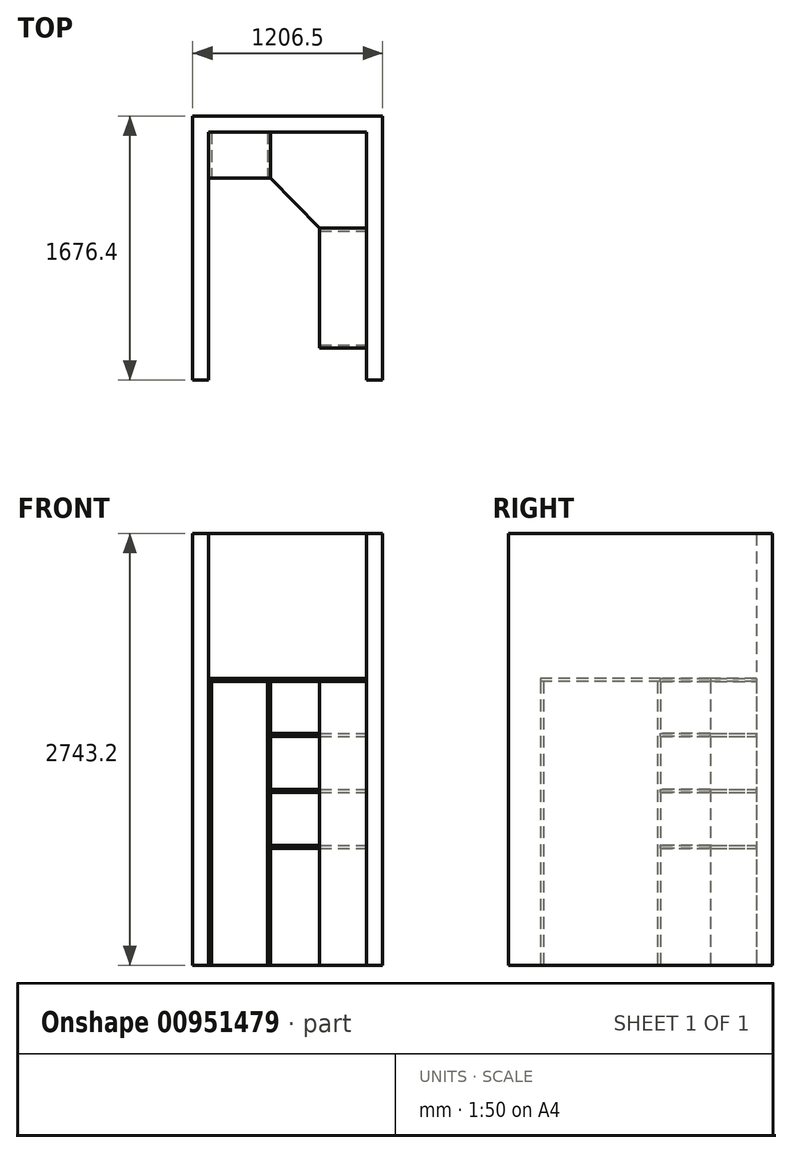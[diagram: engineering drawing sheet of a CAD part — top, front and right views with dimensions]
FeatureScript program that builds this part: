
annotation { "Feature Type Name" : "Feature", "Feature Type Description" : "" }
export const myFeature = defineFeature(function(context is Context, id is Id, definition is map)
    precondition{}
    {
        {
            var Q0;
            Q0=qCreatedBy(makeId("Top.planeOp"),FACE);
            var sketch = newSketch(context, id + "F0", { "sketchPlane" : qUnion([Q0])});
            skLineSegment(sketch, "E0.top", {"start": v(0, 1574.8) * mm, "end": v(1003.3, 1574.8) * mm});
            skLineSegment(sketch, "E0.left", {"start": v(0, 0) * mm, "end": v(0, 1574.8) * mm});
            skLineSegment(sketch, "E0.right", {"start": v(1003.3, 0) * mm, "end": v(1003.3, 1574.8) * mm});
            skLineSegment(sketch, "E1.0", {"start": v(-101.6, 0) * mm, "end": v(-101.6, 1676.4) * mm});
            skLineSegment(sketch, "E2.0", {"start": v(-101.6, 1676.4) * mm, "end": v(1104.9, 1676.4) * mm});
            skLineSegment(sketch, "E3.0", {"start": v(1104.9, 0) * mm, "end": v(1104.9, 1676.4) * mm});
            skLineSegment(sketch, "E4", {"start": v(1003.3, 0) * mm, "end": v(1104.9, 0) * mm});
            skLineSegment(sketch, "E5", {"start": v(0, 0) * mm, "end": v(-101.6, 0) * mm});
            skSolve(sketch);
        }
        {
            var Q0;
            Q0 = qSketchRegion(id + "F0", true);
            extrude(context, id + "F1", {"entities" : qUnion([Q0]), "depth" : 2743.2 * mm, "offsetDistance" : 25.4 * mm});
        }
        {
            var Q0;
            Q0=qCreatedBy(makeId("Top.planeOp"),FACE);
            var sketch = newSketch(context, id + "F2", { "sketchPlane" : qUnion([Q0])});
            skLineSegment(sketch, "E6.bottom", {"start": v(0, 1574.8) * mm, "end": v(19.05, 1574.8) * mm});
            skLineSegment(sketch, "E6.top", {"start": v(0, 1282.7) * mm, "end": v(19.05, 1282.7) * mm});
            skLineSegment(sketch, "E6.left", {"start": v(0, 1574.8) * mm, "end": v(0, 1282.7) * mm});
            skLineSegment(sketch, "E6.right", {"start": v(19.05, 1574.8) * mm, "end": v(19.05, 1282.7) * mm});
            skLineSegment(sketch, "E7.bottom", {"start": v(374.65, 1574.8) * mm, "end": v(393.7, 1574.8) * mm});
            skLineSegment(sketch, "E7.top", {"start": v(374.65, 1282.7) * mm, "end": v(393.7, 1282.7) * mm});
            skLineSegment(sketch, "E7.left", {"start": v(374.65, 1574.8) * mm, "end": v(374.65, 1282.7) * mm});
            skLineSegment(sketch, "E7.right", {"start": v(393.7, 1574.8) * mm, "end": v(393.7, 1282.7) * mm});
            skSolve(sketch);
        }
        {
            var Q0;
            Q0 = qSketchRegion(id + "F2", true);
            extrude(context, id + "F3", {"entities" : qUnion([Q0]), "depth" : 1803.4 * mm, "offsetDistance" : 25.4 * mm});
        }
        {
            var Q0;
            Q0=makeQuery(id+"F3.opExtrude","CAP_FACE",FACE,{"disambiguationData":[OSD([sQuery(id+"F2.wireOp",EDGE,"E6.bottom"),sQuery(id+"F2.wireOp",EDGE,"E6.top"),sQuery(id+"F2.wireOp",EDGE,"E6.left"),sQuery(id+"F2.wireOp",EDGE,"E6.right")])],"isStart":false});
            var sketch = newSketch(context, id + "F4", { "sketchPlane" : qUnion([Q0])});
            skLineSegment(sketch, "E8.bottom", {"start": v(0, 1282.7) * mm, "end": v(393.7, 1282.7) * mm});
            skLineSegment(sketch, "E8.top", {"start": v(0, 1574.8) * mm, "end": v(393.7, 1574.8) * mm});
            skLineSegment(sketch, "E8.left", {"start": v(0, 1282.7) * mm, "end": v(0, 1574.8) * mm});
            skLineSegment(sketch, "E8.right", {"start": v(393.7, 1282.7) * mm, "end": v(393.7, 1574.8) * mm});
            skSolve(sketch);
        }
        {
            var Q0;
            Q0 = qSketchRegion(id + "F4", true);
            extrude(context, id + "F5", {"entities" : qUnion([Q0]), "depth" : 19.05 * mm, "offsetDistance" : 25.4 * mm});
        }
        {
            var Q0;
            Q0=qCreatedBy(makeId("Top.planeOp"),FACE);
            var sketch = newSketch(context, id + "F6", { "sketchPlane" : qUnion([Q0])});
            skLineSegment(sketch, "E9.bottom", {"start": v(704.85, 965.2) * mm, "end": v(1003.3, 965.2) * mm});
            skLineSegment(sketch, "E9.top", {"start": v(704.85, 946.15) * mm, "end": v(1003.3, 946.15) * mm});
            skLineSegment(sketch, "E9.left", {"start": v(704.85, 965.2) * mm, "end": v(704.85, 946.15) * mm});
            skLineSegment(sketch, "E9.right", {"start": v(1003.3, 965.2) * mm, "end": v(1003.3, 946.15) * mm});
            skLineSegment(sketch, "E10.bottom", {"start": v(704.85, 222.25) * mm, "end": v(1003.3, 222.25) * mm});
            skLineSegment(sketch, "E10.top", {"start": v(704.85, 203.2) * mm, "end": v(1003.3, 203.2) * mm});
            skLineSegment(sketch, "E10.left", {"start": v(704.85, 222.25) * mm, "end": v(704.85, 203.2) * mm});
            skLineSegment(sketch, "E10.right", {"start": v(1003.3, 222.25) * mm, "end": v(1003.3, 203.2) * mm});
            skSolve(sketch);
        }
        {
            var Q0;
            Q0 = qSketchRegion(id + "F6", true);
            extrude(context, id + "F7", {"entities" : qUnion([Q0]), "depth" : 1803.4 * mm, "offsetDistance" : 25.4 * mm});
        }
        {
            var Q0;
            Q0=makeQuery(id+"F7.opExtrude","CAP_FACE",FACE,{"disambiguationData":[OSD([sQuery(id+"F6.wireOp",EDGE,"E9.bottom"),sQuery(id+"F6.wireOp",EDGE,"E9.top"),sQuery(id+"F6.wireOp",EDGE,"E9.left"),sQuery(id+"F6.wireOp",EDGE,"E9.right")])],"isStart":false});
            var sketch = newSketch(context, id + "F8", { "sketchPlane" : qUnion([Q0])});
            skLineSegment(sketch, "E11.bottom", {"start": v(704.85, 965.2) * mm, "end": v(1003.3, 965.2) * mm});
            skLineSegment(sketch, "E11.top", {"start": v(704.85, 203.2) * mm, "end": v(1003.3, 203.2) * mm});
            skLineSegment(sketch, "E11.left", {"start": v(704.85, 965.2) * mm, "end": v(704.85, 203.2) * mm});
            skLineSegment(sketch, "E11.right", {"start": v(1003.3, 965.2) * mm, "end": v(1003.3, 203.2) * mm});
            skSolve(sketch);
        }
        {
            var Q0;
            Q0 = qSketchRegion(id + "F8", true);
            extrude(context, id + "F9", {"entities" : qUnion([Q0]), "depth" : 19.05 * mm, "offsetDistance" : 25.4 * mm});
        }
        {
            var Q0;
            Q0=makeQuery(id+"F5.opExtrude","CAP_FACE",FACE,{"disambiguationData":[OSD([sQuery(id+"F4.wireOp",EDGE,"E8.bottom"),sQuery(id+"F4.wireOp",EDGE,"E8.top"),sQuery(id+"F4.wireOp",EDGE,"E8.left"),sQuery(id+"F4.wireOp",EDGE,"E8.right")])],"isStart":false});
            var sketch = newSketch(context, id + "F10", { "sketchPlane" : qUnion([Q0])});
            skLineSegment(sketch, "E12.0", {"start": v(393.7, 1282.7) * mm, "end": v(393.7, 1574.8) * mm});
            skLineSegment(sketch, "E12.1", {"start": v(393.7, 1574.8) * mm, "end": v(1003.3, 1574.8) * mm});
            skLineSegment(sketch, "E12.2", {"start": v(1003.3, 965.2) * mm, "end": v(1003.3, 1574.8) * mm});
            skLineSegment(sketch, "E12.3", {"start": v(704.85, 965.2) * mm, "end": v(1003.3, 965.2) * mm});
            skLineSegment(sketch, "E13", {"start": v(393.7, 1282.7) * mm, "end": v(704.85, 965.2) * mm});
            skPoint(sketch, "E14.orphan", {"position": v(0, 1574.8) * mm});
            skPoint(sketch, "E15.orphan", {"position": v(1003.3, 0) * mm});
            skSolve(sketch);
        }
        {
            var Q0;
            Q0 = qSketchRegion(id + "F10", true);
            extrude(context, id + "F11", {"entities" : qUnion([Q0]), "oppositeDirection" : true, "depth" : 19.05 * mm, "offsetDistance" : 25.4 * mm});
        }
        {
            var Q0;
            Q0=makeQuery(id+"F11.opExtrude","SWEPT_BODY",BODY,{"disambiguationData":[OSD([sQuery(id+"F10.wireOp",EDGE,"E12.0"),sQuery(id+"F10.wireOp",EDGE,"E12.1"),sQuery(id+"F10.wireOp",EDGE,"E12.2"),sQuery(id+"F10.wireOp",EDGE,"E12.3"),sQuery(id+"F10.wireOp",EDGE,"E13")])]});
            var Q1;
            Q1=makeQuery(id+"F1.opExtrude","SWEPT_EDGE",EDGE,{"disambiguationData":[OSD([sQuery(id+"F0.wireOp",EDGE,"E0.top"),sQuery(id+"F0.wireOp",EDGE,"E0.right")])]});
            transform(context, id + "F12", {"entities" : qUnion([Q0]), "transformType" : TransformType.TRANSLATION_3D, "dx" : 0 * mm, "dy" : 0 * mm, "dz" : -1059.18 * mm, "makeCopy" : true});
        }
        {
            var Q0;
            Q0=makeQuery(id+"F12.opPattern","COPY",BODY,{"derivedFrom":makeQuery(id+"F11.opExtrude","SWEPT_BODY",BODY,{"disambiguationData":[OSD([sQuery(id+"F10.wireOp",EDGE,"E12.0"),sQuery(id+"F10.wireOp",EDGE,"E12.1"),sQuery(id+"F10.wireOp",EDGE,"E12.2"),sQuery(id+"F10.wireOp",EDGE,"E12.3"),sQuery(id+"F10.wireOp",EDGE,"E13")])]}),"instanceName":"1"});
            transform(context, id + "F13", {"entities" : qUnion([Q0]), "transformType" : TransformType.TRANSLATION_3D, "dx" : 0 * mm, "dy" : 0 * mm, "dz" : 355.6 * mm, "makeCopy" : true});
        }
        {
            var Q0;
            Q0=makeQuery(id+"F13.opPattern","COPY",BODY,{"derivedFrom":makeQuery(id+"F12.opPattern","COPY",BODY,{"derivedFrom":makeQuery(id+"F11.opExtrude","SWEPT_BODY",BODY,{"disambiguationData":[OSD([sQuery(id+"F10.wireOp",EDGE,"E12.0"),sQuery(id+"F10.wireOp",EDGE,"E12.1"),sQuery(id+"F10.wireOp",EDGE,"E12.2"),sQuery(id+"F10.wireOp",EDGE,"E12.3"),sQuery(id+"F10.wireOp",EDGE,"E13")])]}),"instanceName":"1"}),"instanceName":"1"});
            transform(context, id + "F14", {"entities" : qUnion([Q0]), "transformType" : TransformType.TRANSLATION_3D, "dx" : 0 * mm, "dy" : 0 * mm, "dz" : 355.6 * mm, "makeCopy" : true});
        }
    });
